# Revit family: Ivar Arm Chair
name_source: partatom
category: Furniture
revit_build: Autodesk Revit 2017 (Build: 20160225_1515(x64)
units: mm (PartAtom-declared; Revit-internal decimal feet)

## family parameters
Always vertical = Yes
Cut with Voids When Loaded = No
OmniClass Number = 23.40.20.00
OmniClass Title = General Furniture and Specialties
Room Calculation Point = No
Shared = No
Work Plane-Based = No

## types (1)
- Ivar Arm Chair
    Armrest height = 26 mm
    Assembly Code = E2020200
    Assistance = Call for assistance number: 336.941.3446
    Chair type = Arm
    Collection = Ivar
    Depth = 24 mm
    Description = Wood frame, upholstered seat and upholstered outside and inside back
    Height = 34 mm
    Industry = Café, Restaurant, Bistro, Lounge, Hotel, Club, Assisted Living
    Length = 23 mm  [stored 0.0754593 ft]
    Manufacturer = Beaufurn
    Manufacturer Country = USA
    Model = Ivar Arm Chair
    Products of collection = Ivar Stacking Side Chair and Ivar Barstool
    Seat height = 19 mm
    Structure material = Standard wood finishes or Cof
    Type Comments = Suitable for use in many commercial seating applications such as restaurant seating, bar room furniture, waiting room chairs or club seating
    URL = http://beaufurn.com
    Upholstery material = Graded Fabric or Com
    Usage = Indoor
    Yardage = 1 mm  [stored 0.00328084 ft]

note: [stored X ft] marks values corroborated as IEEE doubles in the binary element streams (Revit-internal decimal feet)

## geometry (parser evidence)
native form markers: Sweep x3
no freeform markers — native parametric forms only
